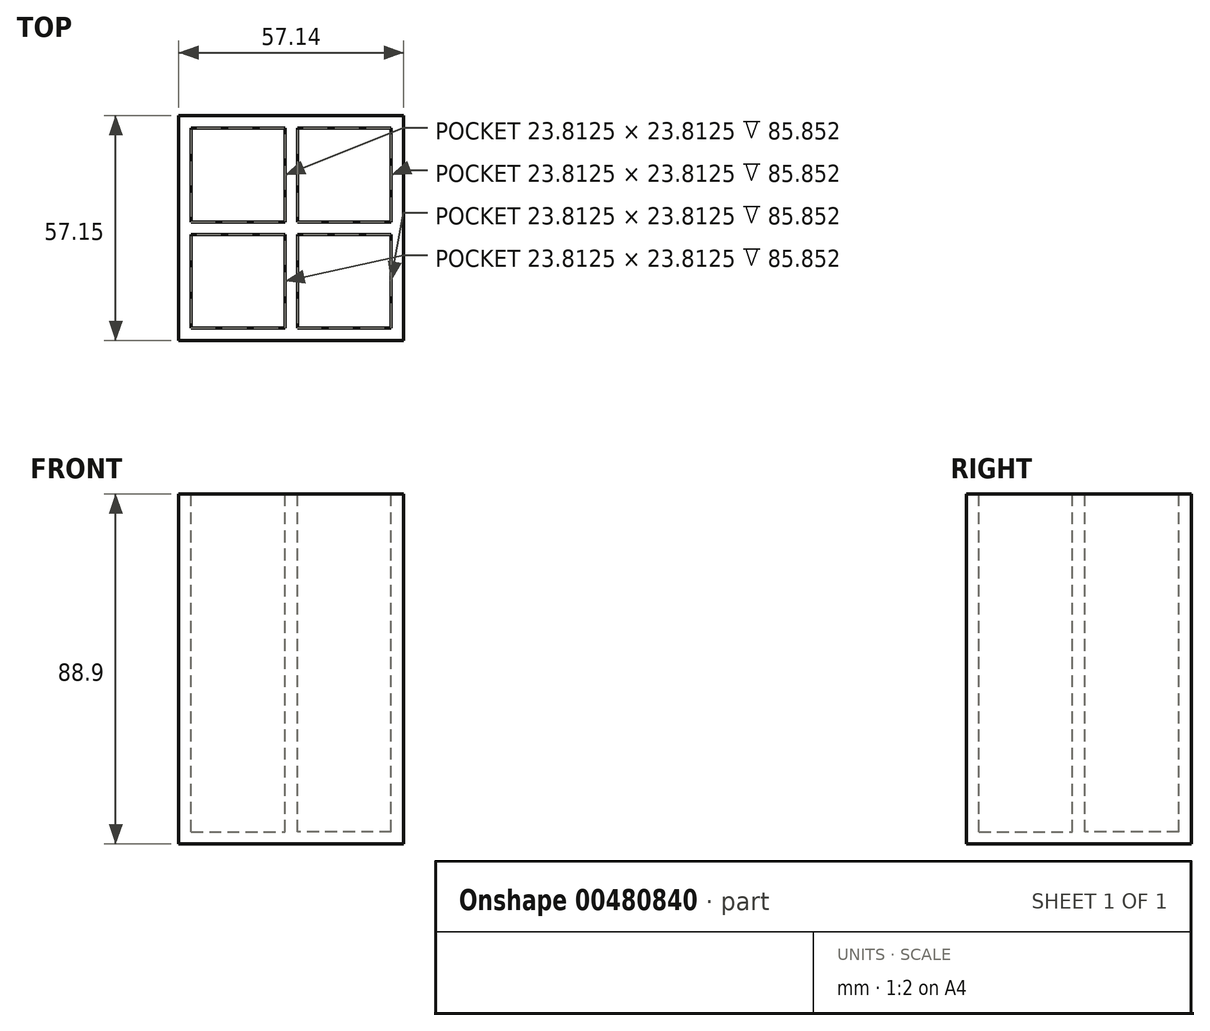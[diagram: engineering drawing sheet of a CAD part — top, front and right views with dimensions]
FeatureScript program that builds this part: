
annotation { "Feature Type Name" : "Feature", "Feature Type Description" : "" }
export const myFeature = defineFeature(function(context is Context, id is Id, definition is map)
    precondition{}
    {
        {
            var Q0;
            Q0=qCreatedBy(makeId("Front.planeOp"),FACE);
            var sketch = newSketch(context, id + "F0", { "sketchPlane" : qUnion([Q0])});
            skLineSegment(sketch, "E0.bottom", {"start": v(-28.58, -44.45) * mm, "end": v(28.58, -44.45) * mm});
            skLineSegment(sketch, "E0.top", {"start": v(-28.58, 44.45) * mm, "end": v(28.58, 44.45) * mm});
            skLineSegment(sketch, "E0.left", {"start": v(-28.58, -44.45) * mm, "end": v(-28.57, 44.45) * mm});
            skLineSegment(sketch, "E0.right", {"start": v(28.57, -44.45) * mm, "end": v(28.58, 44.45) * mm});
            skPoint(sketch, "E0.middle", {"position": v(0, 0) * mm});
            skSolve(sketch);
        }
        {
            var Q0;
            Q0=makeQuery(id+"F0.imprint","IMPRINT",FACE,{"disambiguationData":[TD([[makeQuery(id+"F0.imprint","IMPRINT",EDGE,{"derivedFrom":sQuery(id+"F0.wireOp",EDGE,"E0.bottom")}),1.0]])]});
            extrude(context, id + "F1", {"entities" : qUnion([Q0]), "depth" : 57.15 * mm});
        }
        {
            var Q0;
            Q0=makeQuery(id+"F1.opExtrude","SWEPT_FACE",FACE,{"disambiguationData":[OSD([sQuery(id+"F0.wireOp",EDGE,"E0.top")])]});
            var sketch = newSketch(context, id + "F2", { "sketchPlane" : qUnion([Q0])});
            skLineSegment(sketch, "E1.bottom", {"start": v(-25.4, -3.18) * mm, "end": v(-1.59, -3.17) * mm});
            skLineSegment(sketch, "E1.top", {"start": v(-25.4, -26.99) * mm, "end": v(-1.59, -26.99) * mm});
            skLineSegment(sketch, "E1.left", {"start": v(-25.4, -3.18) * mm, "end": v(-25.4, -26.99) * mm});
            skLineSegment(sketch, "E1.right", {"start": v(-1.59, -3.17) * mm, "end": v(-1.59, -26.99) * mm});
            skLineSegment(sketch, "E2.bottom", {"start": v(25.4, -3.17) * mm, "end": v(1.59, -3.18) * mm});
            skLineSegment(sketch, "E2.top", {"start": v(25.4, -26.99) * mm, "end": v(1.59, -26.99) * mm});
            skLineSegment(sketch, "E2.left", {"start": v(25.4, -3.17) * mm, "end": v(25.4, -26.99) * mm});
            skLineSegment(sketch, "E2.right", {"start": v(1.59, -3.18) * mm, "end": v(1.59, -26.99) * mm});
            skLineSegment(sketch, "E3.bottom", {"start": v(25.4, -53.98) * mm, "end": v(1.59, -53.98) * mm});
            skLineSegment(sketch, "E3.top", {"start": v(25.4, -30.16) * mm, "end": v(1.59, -30.16) * mm});
            skLineSegment(sketch, "E3.left", {"start": v(25.4, -53.98) * mm, "end": v(25.4, -30.16) * mm});
            skLineSegment(sketch, "E3.right", {"start": v(1.59, -53.98) * mm, "end": v(1.59, -30.16) * mm});
            skLineSegment(sketch, "E4.bottom", {"start": v(-25.4, -53.98) * mm, "end": v(-1.59, -53.98) * mm});
            skLineSegment(sketch, "E4.top", {"start": v(-25.4, -30.16) * mm, "end": v(-1.59, -30.16) * mm});
            skLineSegment(sketch, "E4.left", {"start": v(-25.4, -53.98) * mm, "end": v(-25.4, -30.16) * mm});
            skLineSegment(sketch, "E4.right", {"start": v(-1.59, -53.98) * mm, "end": v(-1.59, -30.16) * mm});
            skSolve(sketch);
        }
        {
            var Q0;
            Q0=makeQuery(id+"F2.imprint","IMPRINT",FACE,{"disambiguationData":[TD([[makeQuery(id+"F2.imprint","IMPRINT",EDGE,{"derivedFrom":sQuery(id+"F2.wireOp",EDGE,"E1.bottom")}),-1.0]])]});
            var Q1;
            Q1=makeQuery(id+"F2.imprint","IMPRINT",FACE,{"disambiguationData":[TD([[makeQuery(id+"F2.imprint","IMPRINT",EDGE,{"derivedFrom":sQuery(id+"F2.wireOp",EDGE,"E2.bottom")}),1.0]])]});
            var Q2;
            Q2=makeQuery(id+"F2.imprint","IMPRINT",FACE,{"disambiguationData":[TD([[makeQuery(id+"F2.imprint","IMPRINT",EDGE,{"derivedFrom":sQuery(id+"F2.wireOp",EDGE,"E3.bottom")}),-1.0]])]});
            var Q3;
            Q3=makeQuery(id+"F2.imprint","IMPRINT",FACE,{"disambiguationData":[TD([[makeQuery(id+"F2.imprint","IMPRINT",EDGE,{"derivedFrom":sQuery(id+"F2.wireOp",EDGE,"E4.bottom")}),1.0]])]});
            extrude(context, id + "F3", {"entities" : qUnion([Q0, Q1, Q2, Q3]), "operationType" : NewBodyOperationType.REMOVE, "oppositeDirection" : true, "depth" : 85.85 * mm});
        }
    });
